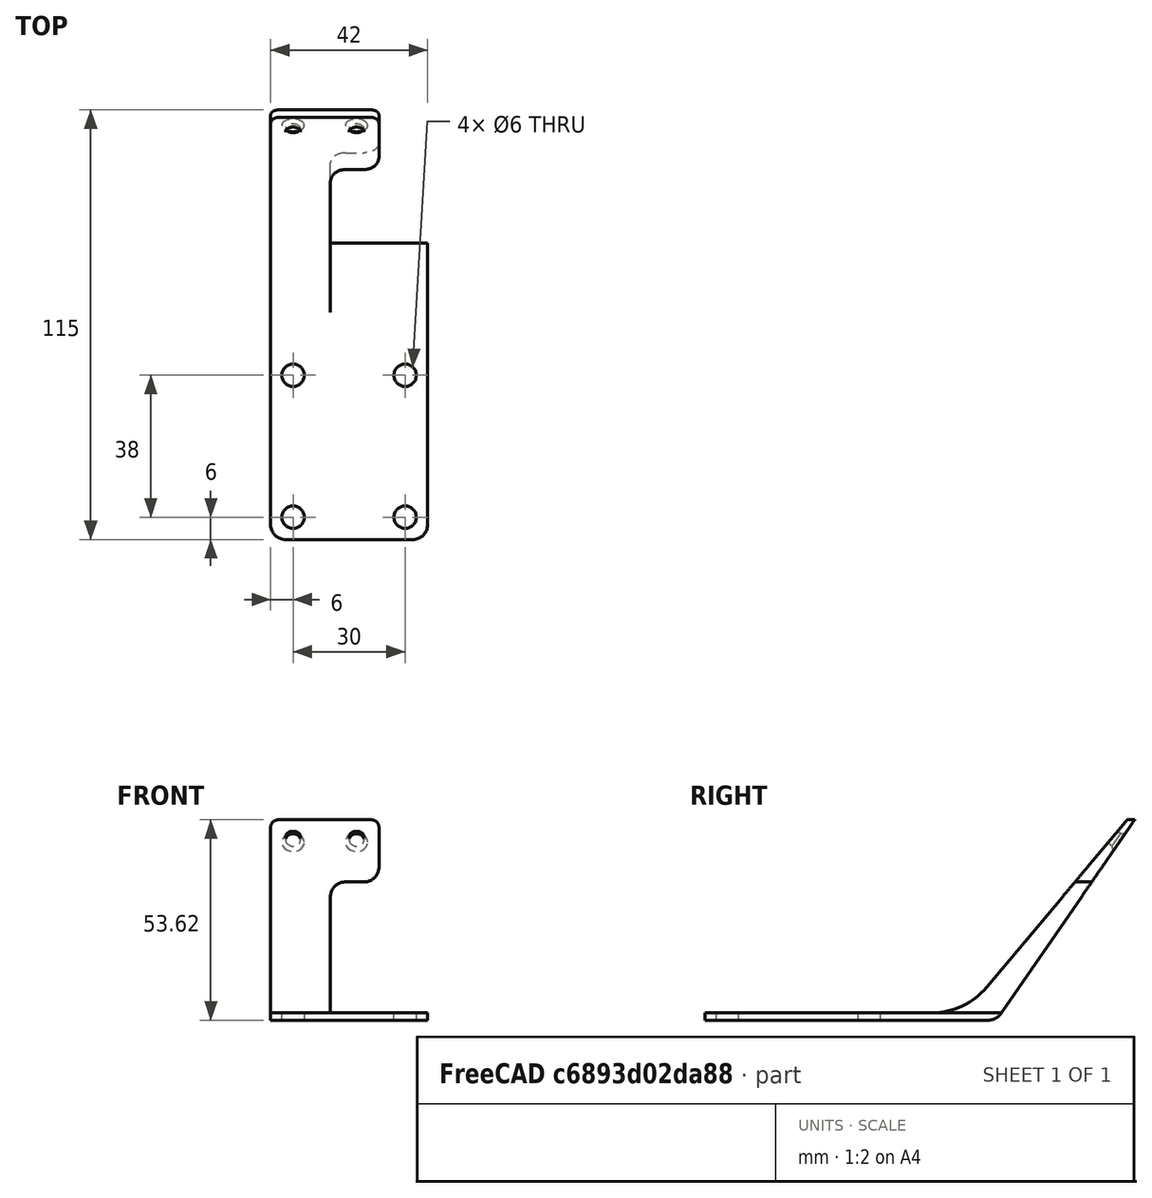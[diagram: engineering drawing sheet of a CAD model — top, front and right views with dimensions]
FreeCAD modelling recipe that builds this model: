
FCSTD DOCUMENT  (FreeCAD 0.17R13528 (Git))
Label: supportBadgeArea
License: All rights reserved
LicenseURL: http://en.wikipedia.org/wiki/All_rights_reserved
objects: PartDesign::Fillet×8, Sketcher::SketchObject×6, PartDesign::Pad×3, PartDesign::Pocket×3, PartDesign::Chamfer×2, PartDesign::Body×1, Mesh::Feature×1
note: 29 computed .brp shape members not serialized (recipe doc carries the construction recipe); baked Part::Feature solids carry a one-line shape summary decoded from their .brp

FEATURE [Sketcher::SketchObject] Sketch
  MapMode = 5
  Support = -> [XY_Plane]
  sketch-geometry (4):
    g0: LineSegment StartX=0 StartY=78 StartZ=0 EndX=42 EndY=78 EndZ=0
    g1: LineSegment StartX=42 StartY=78 StartZ=0 EndX=42 EndY=0 EndZ=0
    g2: LineSegment StartX=42 StartY=0 StartZ=0 EndX=0 EndY=0 EndZ=0
    g3: LineSegment StartX=0 StartY=0 StartZ=0 EndX=0 EndY=78 EndZ=0
  constraints (11):
    c: Coincident(g0,g1)
    c: Coincident(g1,g2)
    c: Coincident(g2,g3)
    c: Coincident(g3,g0)
    c: Horizontal(g0)
    c: Horizontal(g2)
    c: Vertical(g1)
    c: Vertical(g3)
    c: Distance(g2) = 42
    c: Distance(g3) = 78
    c: Coincident(g-1,g2)
FEATURE [PartDesign::Pad] Pad
  Length = 2
  Length2 = 100
  Profile = -> Sketch
  Type = 0
FEATURE [Sketcher::SketchObject] Sketch001
  MapMode = 5
  Placement = pos=(0,0,2) rot=(0,0,1;0rad)
  Support = -> [Pad]
  sketch-geometry (4):
    g0: Circle CenterX=6 CenterY=44 CenterZ=0 NormalX=0 NormalY=0 NormalZ=1 AngleXU=0 Radius=3
    g1: Circle CenterX=36 CenterY=44 CenterZ=0 NormalX=0 NormalY=0 NormalZ=1 AngleXU=0 Radius=3
    g2: Circle CenterX=6 CenterY=6 CenterZ=0 NormalX=0 NormalY=0 NormalZ=1 AngleXU=0 Radius=3
    g3: Circle CenterX=36 CenterY=6 CenterZ=0 NormalX=0 NormalY=0 NormalZ=1 AngleXU=0 Radius=3
  constraints (12):
    c: Radius(g2) = 3
    c: Equal(g2,g3)
    c: Equal(g2,g1)
    c: Equal(g2,g0)
    c: Horizontal(g2,g3)
    c: Horizontal(g0,g1)
    c: Vertical(g1,g3)
    c: Vertical(g0,g2)
    c: DistanceX(g-1,g2) = 6
    c: DistanceY(g-1,g2) = 6
    c: DistanceX(g2,g3) = 30
    c: DistanceY(g2,g0) = 38
FEATURE [PartDesign::Pocket] Pocket
  BaseFeature = -> Pad
  Length = 5
  Length2 = 100
  Profile = -> Sketch001
  Type = 1
FEATURE [Sketcher::SketchObject] Sketch002
  ExternalGeometry = -> [Pocket]
  MapMode = 5
  Placement = pos=(0,0,0) rot=(0.57735,-0.57735,-0.57735;2.0944rad)
  Support = -> [Pocket]
  sketch-geometry (4):
    g0: LineSegment StartX=-78 StartY=0 StartZ=0 EndX=-114.995 EndY=53.6231 EndZ=0
    g1: LineSegment StartX=-114.995 StartY=53.6231 StartZ=0 EndX=-112.995 EndY=53.6231 EndZ=0
    g2: LineSegment StartX=-112.995 StartY=53.6231 StartZ=0 EndX=-68 EndY=0 EndZ=0
    g3: LineSegment StartX=-68 StartY=0 StartZ=0 EndX=-78 EndY=0 EndZ=0
  constraints (11):
    c: Coincident(g0,g1)
    c: Horizontal(g1)
    c: Coincident(g1,g2)
    c: Coincident(g2,g3)
    c: Coincident(g3,g0)
    c: Horizontal(g3)
    c: Distance(g2) = 70
    c: Coincident(g0,g-3)
    c: Angle(g-1,g2) = 2.26893
    c: Distance(g1) = 2
    c: Distance(g3) = 10
FEATURE [PartDesign::Pad] Pad001
  BaseFeature = -> Pocket
  Length = 29
  Length2 = 100
  Profile = -> Sketch002
  Reversed = true
  Type = 0
FEATURE [Sketcher::SketchObject] Sketch003
  ExternalGeometry = -> [Pad001]
  MapMode = 5
  Placement = pos=(0,0,0) rot=(1,0,0;1.5708rad)
  Support = -> [XZ_Plane]
  sketch-geometry (4):
    g0: LineSegment StartX=29 StartY=2 StartZ=0 EndX=16 EndY=2 EndZ=0
    g1: LineSegment StartX=16 StartY=2 StartZ=0 EndX=16 EndY=37 EndZ=0
    g2: LineSegment StartX=16 StartY=37 StartZ=0 EndX=29 EndY=37 EndZ=0
    g3: LineSegment StartX=29 StartY=37 StartZ=0 EndX=29 EndY=2 EndZ=0
  constraints (11):
    c: Coincident(g0,g1)
    c: Coincident(g1,g2)
    c: Coincident(g2,g3)
    c: Coincident(g3,g0)
    c: Horizontal(g0)
    c: Horizontal(g2)
    c: Vertical(g1)
    c: Vertical(g3)
    c: Coincident(g0,g-3)
    c: Distance(g2) = 13
    c: Distance(g3) = 35
FEATURE [PartDesign::Pocket] Pocket001
  BaseFeature = -> Pad001
  Length = 5
  Length2 = 100
  Profile = -> Sketch003
  Type = 1
FEATURE [Sketcher::SketchObject] Sketch004
  ExternalGeometry = -> [Pocket001]
  MapMode = 5
  Placement = pos=(29,0,0) rot=(0.57735,0.57735,0.57735;2.0944rad)
  Support = -> [Pocket001]
  sketch-geometry (3):
    g0: LineSegment StartX=78 StartY=0 StartZ=0 EndX=78 EndY=2 EndZ=0
    g1: LineSegment StartX=78 StartY=2 StartZ=0 EndX=79.3798 EndY=2 EndZ=0
    g2: LineSegment StartX=79.3798 StartY=2 StartZ=0 EndX=78 EndY=0 EndZ=0
  constraints (7):
    c: Coincident(g0,g1)
    c: Horizontal(g1)
    c: Coincident(g1,g2)
    c: Coincident(g2,g0)
    c: Coincident(g0,g-3)
    c: Coincident(g0,g-5)
    c: Coincident(g-4,g1)
FEATURE [PartDesign::Pad] Pad002
  BaseFeature = -> Pocket001
  Length = 13
  Length2 = 100
  Profile = -> Sketch004
  Type = 0
FEATURE [Sketcher::SketchObject] Sketch005
  ExternalGeometry = -> [Pad002]
  MapMode = 5
  Placement = pos=(0,39.904,-33.4835) rot=(1,0,0;0.872665rad)
  Support = -> [Pad002]
  sketch-geometry (2):
    g0: Circle CenterX=6 CenterY=107.71 CenterZ=0 NormalX=0 NormalY=0 NormalZ=1 AngleXU=0 Radius=2
    g1: Circle CenterX=23 CenterY=107.71 CenterZ=0 NormalX=0 NormalY=0 NormalZ=1 AngleXU=0 Radius=2
  constraints (6):
    c: Horizontal(g0,g1)
    c: Radius(g0) = 2
    c: Equal(g0,g1)
    c: DistanceY(g1,g-4) = 6
    c: DistanceX(g-1,g0) = 6
    c: DistanceX(g1,g-4) = 6
FEATURE [PartDesign::Pocket] Pocket002
  BaseFeature = -> Pad002
  Length = 5
  Length2 = 100
  Profile = -> Sketch005
  Type = 1
FEATURE [PartDesign::Chamfer] Chamfer
  Base = -> Pocket002 [Edge24]
  BaseFeature = -> Pocket002
  Size = 1
FEATURE [PartDesign::Chamfer] Chamfer001
  Base = -> Chamfer [Edge10]
  BaseFeature = -> Chamfer
  Size = 1
FEATURE [PartDesign::Fillet] Fillet
  Base = -> Chamfer001 [Edge34]
  BaseFeature = -> Chamfer001
  Radius = 4
FEATURE [PartDesign::Fillet] Fillet001
  Base = -> Fillet [Edge18]
  BaseFeature = -> Fillet
  Radius = 2
FEATURE [PartDesign::Fillet] Fillet002
  Base = -> Fillet001 [Edge15]
  BaseFeature = -> Fillet001
  Radius = 4
FEATURE [PartDesign::Fillet] Fillet003
  Base = -> Fillet002 [Edge23]
  BaseFeature = -> Fillet002
  Radius = 2
FEATURE [PartDesign::Fillet] Fillet004
  Base = -> Fillet003 [Edge6]
  BaseFeature = -> Fillet003
  Radius = 4
FEATURE [PartDesign::Fillet] Fillet005
  Base = -> Fillet004 [Edge78]
  BaseFeature = -> Fillet004
  Radius = 4
FEATURE [PartDesign::Fillet] Fillet006
  Base = -> Fillet005 [Edge11]
  BaseFeature = -> Fillet005
  Radius = 4
FEATURE [PartDesign::Fillet] Fillet007
  Base = -> Fillet006 [Edge23]
  BaseFeature = -> Fillet006
  Radius = 19
FEATURE [PartDesign::Body] Body
  Group = -> [Sketch,Pad,Sketch001,Pocket,Sketch002,Pad001,Sketch003,Pocket001,Sketch004,Pad002,Sketch005,Pocket002,Chamfer,Chamfer001,Fillet,Fillet001,Fillet002,Fillet003,Fillet004,Fillet005,Fillet006,Fillet007]
  Origin = -> Origin
  Tip = -> Fillet007
FEATURE [Mesh::Feature] Mesh  label="Body (Meshed)"
